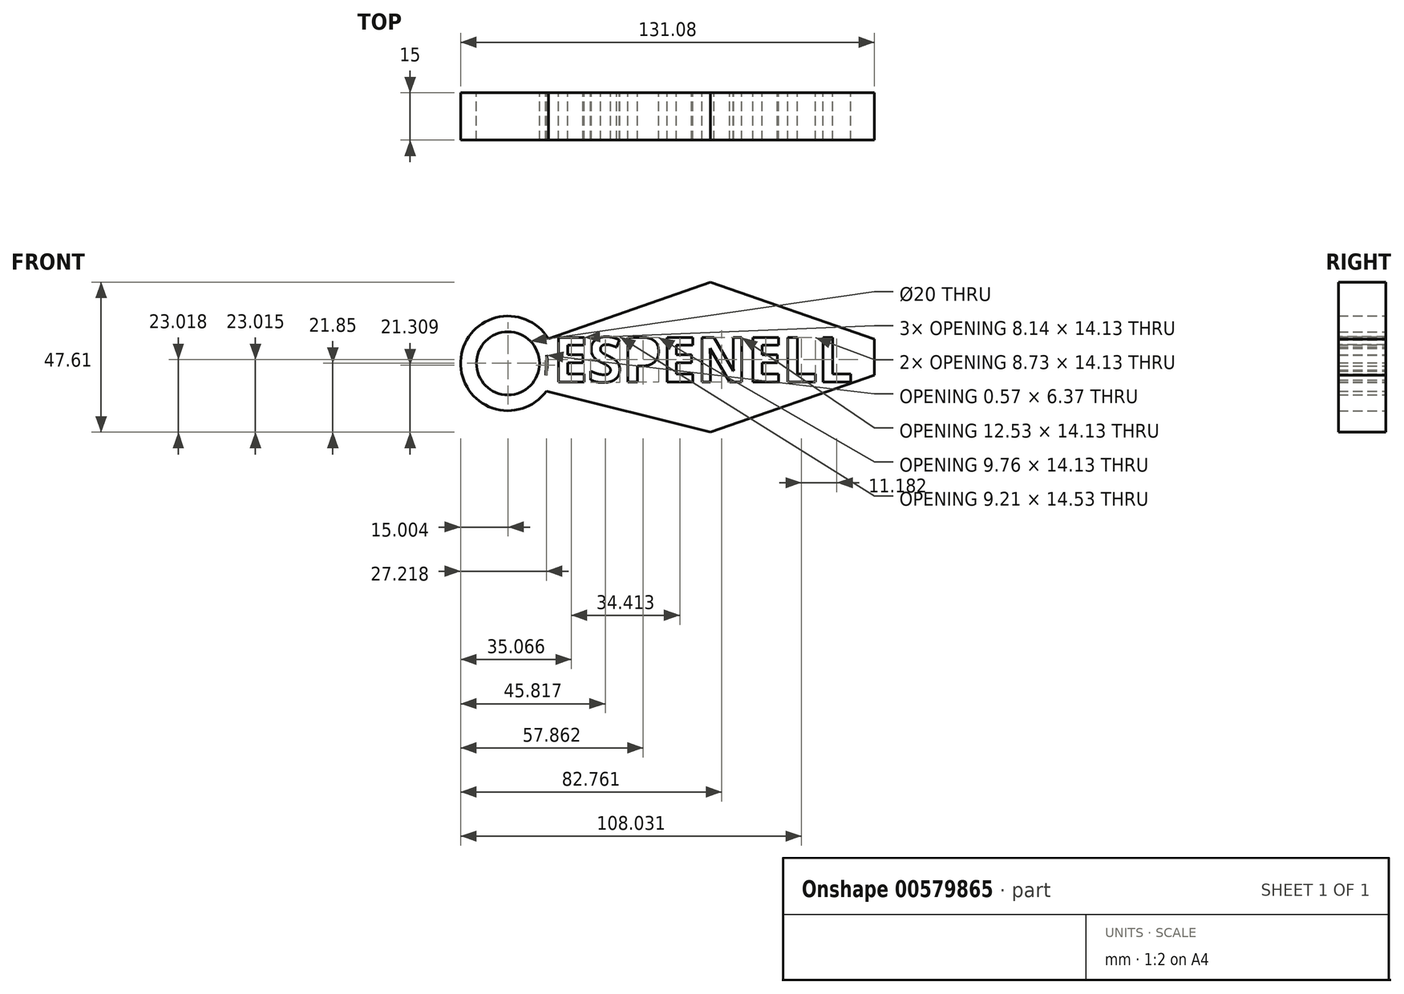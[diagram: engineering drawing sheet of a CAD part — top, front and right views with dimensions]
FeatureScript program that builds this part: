
annotation { "Feature Type Name" : "Feature", "Feature Type Description" : "" }
export const myFeature = defineFeature(function(context is Context, id is Id, definition is map)
    precondition{}
    {
        {
            var Q0;
            Q0=qCreatedBy(makeId("Front.planeOp"),FACE);
            var sketch = newSketch(context, id + "F0", { "sketchPlane" : qUnion([Q0])});
            skArc(sketch, "E0", {"start": v(-52.21, -3.73) * mm, "mid": v(-51.66, -0.56) * mm, "end": v(-51.93, 2.64) * mm});
            skLineSegment(sketch, "E1", {"start": v(-52.21, -3.73) * mm, "end": v(-52.21, -8.73) * mm});
            skLineSegment(sketch, "E2", {"start": v(-51.93, 2.64) * mm, "end": v(-51.93, 7.64) * mm});
            skLineSegment(sketch, "E3", {"start": v(-51.93, 7.64) * mm, "end": v(0, 25.76) * mm});
            skLineSegment(sketch, "E4", {"start": v(0, 25.76) * mm, "end": v(51.93, 7.64) * mm});
            skLineSegment(sketch, "E5", {"start": v(51.93, 7.64) * mm, "end": v(51.93, -3.73) * mm});
            skLineSegment(sketch, "E6", {"start": v(-51.93, 2.64) * mm, "end": v(-52.21, -3.73) * mm});
            skPoint(sketch, "E7.end.orphan", {"position": v(0, -21.85) * mm});
            skLineSegment(sketch, "E8", {"start": v(51.93, -3.73) * mm, "end": v(0, -21.85) * mm});
            skLineSegment(sketch, "E9", {"start": v(0, -21.85) * mm, "end": v(-52.21, -8.73) * mm});
            skText(sketch, "E10", { "text": "ESPENELL", "fontName": "OpenSans-Bold.ttf"});
            skCircle(sketch, "E11", {"center": v(-64.15, 0) * mm, "radius": 15 * mm});
            skCircle(sketch, "E12", {"center": v(-64.15, 0) * mm, "radius": 10 * mm});
            const initialGuessF0  = {"E10": [-0.04993, -0.0059, 1, 0, 0.01425]};
            skSetInitialGuess(sketch, initialGuessF0);
            skSolve(sketch);
        }
        {
            var Q0;
            Q0 = qSketchRegion(id + "F0", true);
            extrude(context, id + "F1", {"entities" : qUnion([Q0]), "depth" : 15 * mm, "offsetDistance" : 25 * mm});
        }
    });
